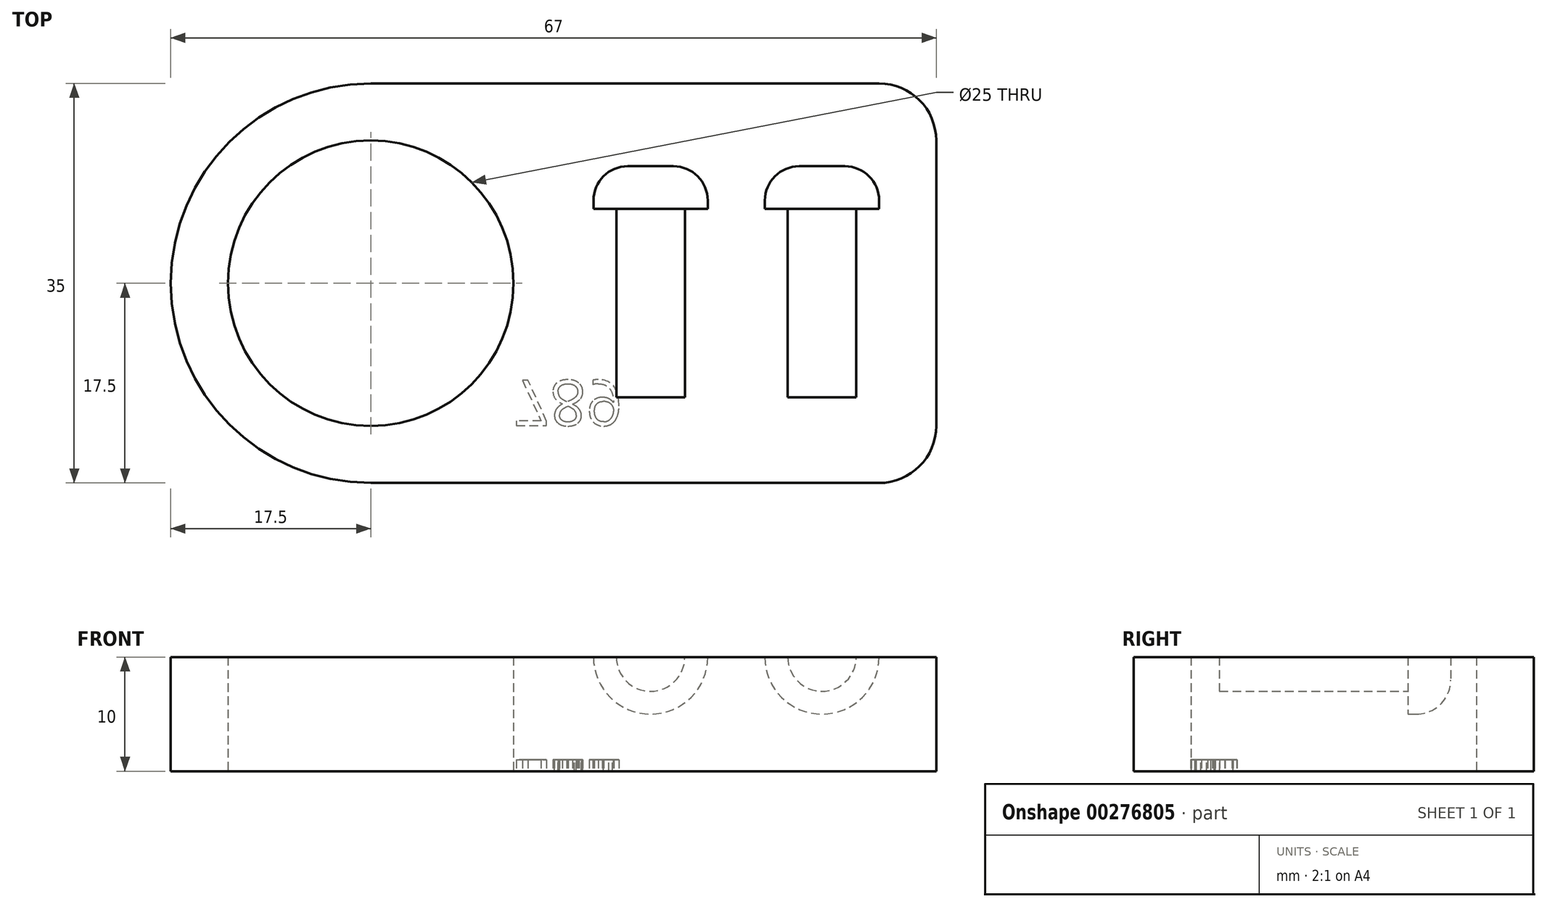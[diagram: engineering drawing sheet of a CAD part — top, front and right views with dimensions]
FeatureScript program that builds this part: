
annotation { "Feature Type Name" : "Feature", "Feature Type Description" : "" }
export const myFeature = defineFeature(function(context is Context, id is Id, definition is map)
    precondition{}
    {
        {
            var Q0;
            Q0=qCreatedBy(makeId("Top.planeOp"),FACE);
            var sketch = newSketch(context, id + "F0", { "sketchPlane" : qUnion([Q0])});
            skLineSegment(sketch, "E0.bottom", {"start": v(17.5, 0) * mm, "end": v(62, 0) * mm});
            skLineSegment(sketch, "E0.top", {"start": v(17.5, 35) * mm, "end": v(62, 35) * mm});
            skLineSegment(sketch, "E0.left", {"start": v(0, 17.5) * mm, "end": v(0, 17.5) * mm});
            skLineSegment(sketch, "E0.right", {"start": v(67, 5) * mm, "end": v(67, 30) * mm});
            skLineSegment(sketch, "E1.bottom", {"start": v(0, 0) * mm, "end": v(17.5, 0) * mm, "construction": true});
            skLineSegment(sketch, "E1.top", {"start": v(0, 17.5) * mm, "end": v(17.5, 17.5) * mm, "construction": true});
            skLineSegment(sketch, "E1.left", {"start": v(0, 0) * mm, "end": v(0, 17.5) * mm, "construction": true});
            skLineSegment(sketch, "E1.right", {"start": v(17.5, 0) * mm, "end": v(17.5, 17.5) * mm, "construction": true});
            skCircle(sketch, "E2", {"center": v(17.5, 17.5) * mm, "radius": 12.5 * mm});
            skPoint(sketch, "E3.visualSharp", {"position": v(0, 0) * mm});
            skArc(sketch, "E3.filletArc", {"start": v(0, 17.5) * mm, "mid": v(5.13, 5.13) * mm, "end": v(17.5, 0) * mm});
            skPoint(sketch, "E4.visualSharp", {"position": v(0, 35) * mm});
            skArc(sketch, "E4.filletArc", {"start": v(17.5, 35) * mm, "mid": v(5.13, 29.87) * mm, "end": v(0, 17.5) * mm});
            skPoint(sketch, "E5.visualSharp", {"position": v(67, 35) * mm});
            skArc(sketch, "E5.filletArc", {"start": v(67, 30) * mm, "mid": v(65.54, 33.54) * mm, "end": v(62, 35) * mm});
            skPoint(sketch, "E6.visualSharp", {"position": v(67, 0) * mm});
            skArc(sketch, "E6.filletArc", {"start": v(62, 0) * mm, "mid": v(65.54, 1.46) * mm, "end": v(67, 5) * mm});
            skSolve(sketch);
        }
        {
            var Q0;
            Q0=makeQuery(id+"F0.imprint","IMPRINT",FACE,{"disambiguationData":[TD([[makeQuery(id+"F0.imprint","IMPRINT",EDGE,{"derivedFrom":sQuery(id+"F0.wireOp",EDGE,"E0.bottom")}),1.0]])]});
            extrude(context, id + "F1", {"entities" : qUnion([Q0]), "depth" : 10 * mm});
        }
        {
            var Q0;
            Q0=makeQuery(id+"F1.opExtrude","CAP_FACE",FACE,{"disambiguationData":[OSD([sQuery(id+"F0.wireOp",EDGE,"E0.bottom"),sQuery(id+"F0.wireOp",EDGE,"E0.top"),sQuery(id+"F0.wireOp",EDGE,"E0.right"),sQuery(id+"F0.wireOp",EDGE,"E2"),sQuery(id+"F0.wireOp",EDGE,"E3.filletArc"),sQuery(id+"F0.wireOp",EDGE,"E4.filletArc"),sQuery(id+"F0.wireOp",EDGE,"E5.filletArc"),sQuery(id+"F0.wireOp",EDGE,"E6.filletArc")])],"isStart":false});
            var sketch = newSketch(context, id + "F2", { "sketchPlane" : qUnion([Q0])});
            skLineSegment(sketch, "E7.bottom", {"start": v(0, 0) * mm, "end": v(42, 0) * mm, "construction": true});
            skLineSegment(sketch, "E7.top", {"start": v(0, 7.5) * mm, "end": v(42, 7.5) * mm, "construction": true});
            skLineSegment(sketch, "E7.left", {"start": v(0, 0) * mm, "end": v(0, 7.5) * mm, "construction": true});
            skLineSegment(sketch, "E7.right", {"start": v(42, 0) * mm, "end": v(42, 7.5) * mm, "construction": true});
            skLineSegment(sketch, "E8.bottom", {"start": v(42, 7.5) * mm, "end": v(45, 7.5) * mm});
            skLineSegment(sketch, "E8.left", {"start": v(42, 7.5) * mm, "end": v(42, 24) * mm});
            skLineSegment(sketch, "E8.right", {"start": v(45, 7.5) * mm, "end": v(45, 24) * mm});
            skLineSegment(sketch, "E9.bottom", {"start": v(45, 24) * mm, "end": v(47, 24) * mm});
            skLineSegment(sketch, "E9.top", {"start": v(42, 27.75) * mm, "end": v(44, 27.75) * mm});
            skLineSegment(sketch, "E9.left", {"start": v(42, 24) * mm, "end": v(42, 27.75) * mm});
            skLineSegment(sketch, "E9.right", {"start": v(47, 24) * mm, "end": v(47, 24.75) * mm});
            skLineSegment(sketch, "E10", {"start": v(42, 7.5) * mm, "end": v(57, 7.5) * mm, "construction": true});
            skPoint(sketch, "E10.endSnap0", {"position": v(43.5, 7.5) * mm});
            skLineSegment(sketch, "E11.bottom", {"start": v(57, 7.5) * mm, "end": v(60, 7.5) * mm});
            skLineSegment(sketch, "E11.left", {"start": v(57, 7.5) * mm, "end": v(57, 24) * mm});
            skLineSegment(sketch, "E11.right", {"start": v(60, 7.5) * mm, "end": v(60, 24) * mm});
            skLineSegment(sketch, "E12.bottom", {"start": v(60, 24) * mm, "end": v(62, 24) * mm});
            skLineSegment(sketch, "E12.top", {"start": v(57, 27.75) * mm, "end": v(59, 27.75) * mm});
            skLineSegment(sketch, "E12.left", {"start": v(57, 24) * mm, "end": v(57, 27.75) * mm});
            skLineSegment(sketch, "E12.right", {"start": v(62, 24) * mm, "end": v(62, 24.75) * mm});
            skPoint(sketch, "E13.visualSharp", {"position": v(47, 27.75) * mm});
            skArc(sketch, "E13.filletArc", {"start": v(47, 24.75) * mm, "mid": v(46.12, 26.87) * mm, "end": v(44, 27.75) * mm});
            skPoint(sketch, "E14.visualSharp", {"position": v(62, 27.75) * mm});
            skArc(sketch, "E14.filletArc", {"start": v(62, 24.75) * mm, "mid": v(61.12, 26.87) * mm, "end": v(59, 27.75) * mm});
            skSolve(sketch);
        }
        {
            var Q0;
            Q0=makeQuery(id+"F2.imprint","IMPRINT",FACE,{"disambiguationData":[TD([[makeQuery(id+"F2.imprint","IMPRINT",EDGE,{"derivedFrom":sQuery(id+"F2.wireOp",EDGE,"E8.bottom")}),1.0]])]});
            var Q1;
            Q1=sQuery(id+"F2.wireOp",EDGE,"E8.left");
            revolve(context, id + "F3", {"operationType" : NewBodyOperationType.REMOVE, "entities" : qUnion([Q0]), "axis" : qUnion([Q1]), "revolveType" : RevolveType.FULL, "oppositeDirection" : true});
        }
        {
            var Q0;
            Q0=makeQuery(id+"F2.imprint","IMPRINT",FACE,{"disambiguationData":[TD([[makeQuery(id+"F2.imprint","IMPRINT",EDGE,{"derivedFrom":sQuery(id+"F2.wireOp",EDGE,"E11.bottom")}),1.0]])]});
            var Q1;
            Q1=sQuery(id+"F2.wireOp",EDGE,"E11.left");
            revolve(context, id + "F4", {"operationType" : NewBodyOperationType.REMOVE, "entities" : qUnion([Q0]), "axis" : qUnion([Q1]), "revolveType" : RevolveType.FULL, "oppositeDirection" : true});
        }
        {
            var Q0;
            Q0=makeQuery(id+"F1.opExtrude","CAP_FACE",FACE,{"disambiguationData":[OSD([sQuery(id+"F0.wireOp",EDGE,"E0.bottom"),sQuery(id+"F0.wireOp",EDGE,"E0.top"),sQuery(id+"F0.wireOp",EDGE,"E0.right"),sQuery(id+"F0.wireOp",EDGE,"E2"),sQuery(id+"F0.wireOp",EDGE,"E3.filletArc"),sQuery(id+"F0.wireOp",EDGE,"E4.filletArc"),sQuery(id+"F0.wireOp",EDGE,"E5.filletArc"),sQuery(id+"F0.wireOp",EDGE,"E6.filletArc")])],"isStart":true});
            var sketch = newSketch(context, id + "F5", { "sketchPlane" : qUnion([Q0])});
            skLineSegment(sketch, "E15.bottom", {"start": v(0, 0) * mm, "end": v(30, 0) * mm, "construction": true});
            skLineSegment(sketch, "E15.top", {"start": v(-5.77, -5) * mm, "end": v(30, -5) * mm, "construction": true});
            skLineSegment(sketch, "E15.left", {"start": v(0, 0) * mm, "end": v(0, -17.5) * mm, "construction": true});
            skLineSegment(sketch, "E15.right", {"start": v(30, 0) * mm, "end": v(30, -5) * mm, "construction": true});
            skText(sketch, "E16", { "text": "789", "fontName": "OpenSans-Regular.ttf"});
            const initialGuessF5  = {"E16": [0.03, -0.009, 1, 0, 0.004]};
            skSetInitialGuess(sketch, initialGuessF5);
            skSolve(sketch);
        }
        {
            var Q0;
            Q0 = qSketchRegion(id + "F5", true);
            extrude(context, id + "F6", {"entities" : qUnion([Q0]), "operationType" : NewBodyOperationType.REMOVE, "oppositeDirection" : true, "depth" : 1 * mm});
        }
    });
